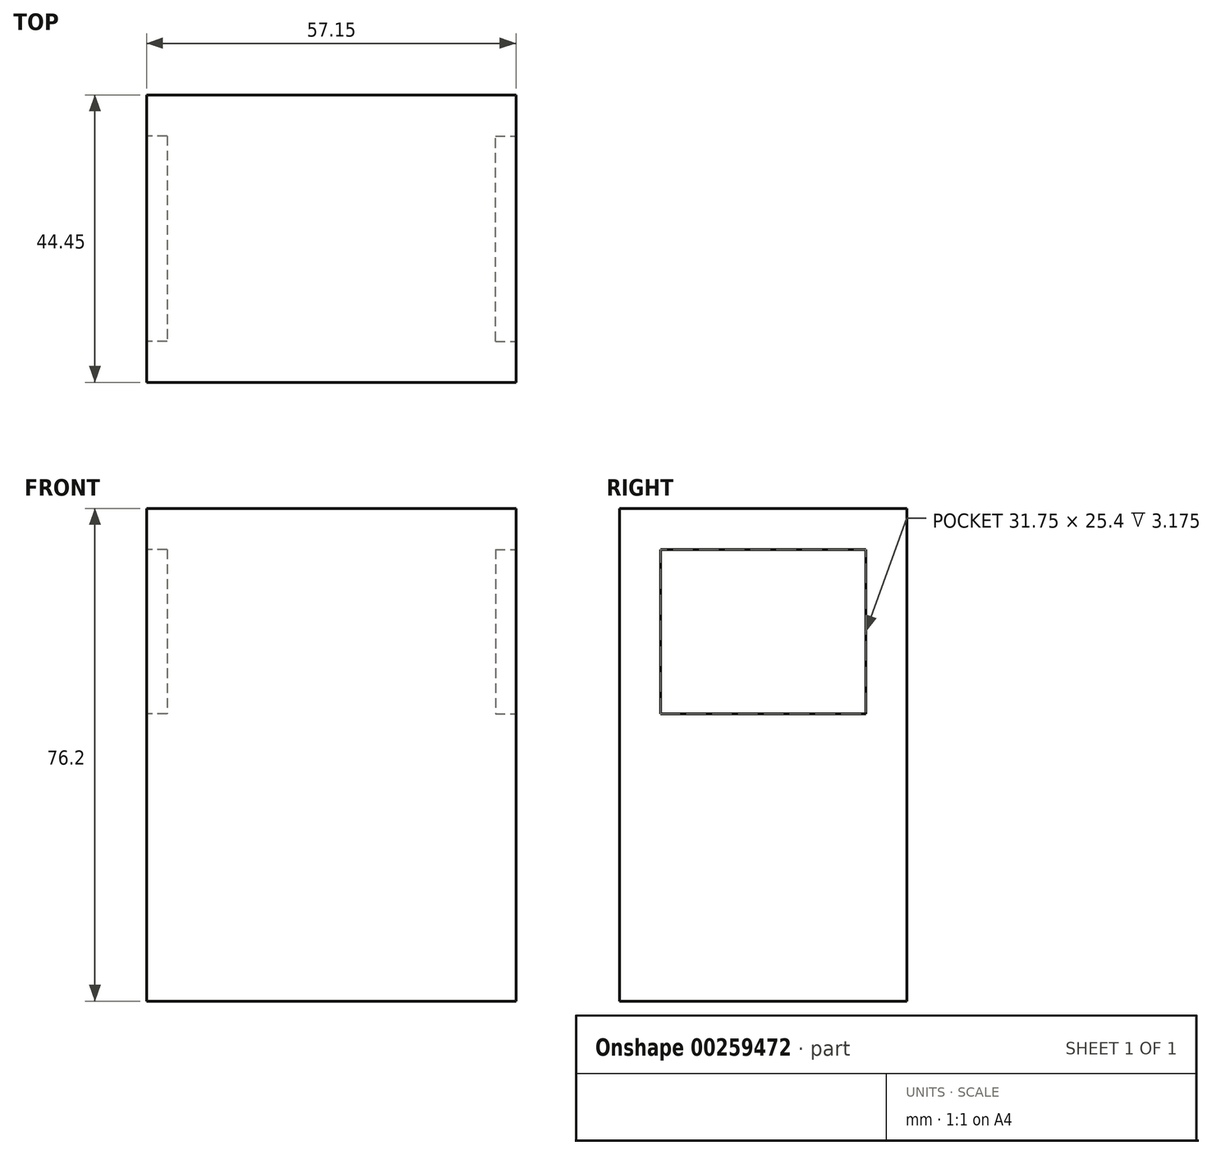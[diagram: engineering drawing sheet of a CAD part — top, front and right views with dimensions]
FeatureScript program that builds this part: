
annotation { "Feature Type Name" : "Feature", "Feature Type Description" : "" }
export const myFeature = defineFeature(function(context is Context, id is Id, definition is map)
    precondition{}
    {
        {
            var Q0;
            Q0=qCreatedBy(makeId("Right.planeOp"),FACE);
            var sketch = newSketch(context, id + "F0", { "sketchPlane" : qUnion([Q0])});
            skLineSegment(sketch, "E0", {"start": v(0, 0) * mm, "end": v(44.45, 0) * mm});
            skLineSegment(sketch, "E1", {"start": v(44.45, 0) * mm, "end": v(44.45, -76.2) * mm});
            skLineSegment(sketch, "E2", {"start": v(44.45, -76.2) * mm, "end": v(0, -76.2) * mm});
            skLineSegment(sketch, "E3", {"start": v(0, -76.2) * mm, "end": v(0, 0) * mm});
            skSolve(sketch);
        }
        {
            var Q0;
            Q0=makeQuery(id+"F0.imprint","IMPRINT",FACE,{"disambiguationData":[TD([[makeQuery(id+"F0.imprint","IMPRINT",EDGE,{"derivedFrom":sQuery(id+"F0.wireOp",EDGE,"E0")}),-1.0]])]});
            extrude(context, id + "F1", {"entities" : qUnion([Q0]), "depth" : 57.15 * mm});
        }
        {
            var Q0;
            Q0=makeQuery(id+"F1.opExtrude","CAP_FACE",FACE,{"disambiguationData":[OSD([sQuery(id+"F0.wireOp",EDGE,"E0"),sQuery(id+"F0.wireOp",EDGE,"E1"),sQuery(id+"F0.wireOp",EDGE,"E2"),sQuery(id+"F0.wireOp",EDGE,"E3")])],"isStart":false});
            var sketch = newSketch(context, id + "F2", { "sketchPlane" : qUnion([Q0])});
            skLineSegment(sketch, "E4.bottom", {"start": v(6.35, -6.35) * mm, "end": v(38.1, -6.35) * mm});
            skLineSegment(sketch, "E4.top", {"start": v(6.35, -31.75) * mm, "end": v(38.1, -31.75) * mm});
            skLineSegment(sketch, "E4.left", {"start": v(6.35, -6.35) * mm, "end": v(6.35, -31.75) * mm});
            skLineSegment(sketch, "E4.right", {"start": v(38.1, -6.35) * mm, "end": v(38.1, -31.75) * mm});
            skSolve(sketch);
        }
        {
            var Q0;
            Q0=makeQuery(id+"F2.imprint","IMPRINT",FACE,{"disambiguationData":[TD([[makeQuery(id+"F2.imprint","IMPRINT",EDGE,{"derivedFrom":sQuery(id+"F2.wireOp",EDGE,"E4.bottom")}),-1.0]])]});
            extrude(context, id + "F3", {"entities" : qUnion([Q0]), "operationType" : NewBodyOperationType.REMOVE, "oppositeDirection" : true, "depth" : 3.17 * mm});
        }
        {
            var Q0;
            Q0=makeQuery(id+"F1.opExtrude","CAP_FACE",FACE,{"disambiguationData":[OSD([sQuery(id+"F0.wireOp",EDGE,"E0"),sQuery(id+"F0.wireOp",EDGE,"E1"),sQuery(id+"F0.wireOp",EDGE,"E2"),sQuery(id+"F0.wireOp",EDGE,"E3")])],"isStart":true});
            var sketch = newSketch(context, id + "F4", { "sketchPlane" : qUnion([Q0])});
            skLineSegment(sketch, "E5.bottom", {"start": v(-38.1, -6.35) * mm, "end": v(-6.35, -6.35) * mm});
            skLineSegment(sketch, "E5.top", {"start": v(-38.1, -31.75) * mm, "end": v(-6.35, -31.75) * mm});
            skLineSegment(sketch, "E5.left", {"start": v(-38.1, -6.35) * mm, "end": v(-38.1, -31.75) * mm});
            skLineSegment(sketch, "E5.right", {"start": v(-6.35, -6.35) * mm, "end": v(-6.35, -31.75) * mm});
            skSolve(sketch);
        }
        {
            var Q0;
            Q0=makeQuery(id+"F4.imprint","IMPRINT",FACE,{"disambiguationData":[TD([[makeQuery(id+"F4.imprint","IMPRINT",EDGE,{"derivedFrom":sQuery(id+"F4.wireOp",EDGE,"E5.bottom")}),-1.0]])]});
            extrude(context, id + "F5", {"entities" : qUnion([Q0]), "operationType" : NewBodyOperationType.REMOVE, "oppositeDirection" : true, "depth" : 3.17 * mm});
        }
    });
